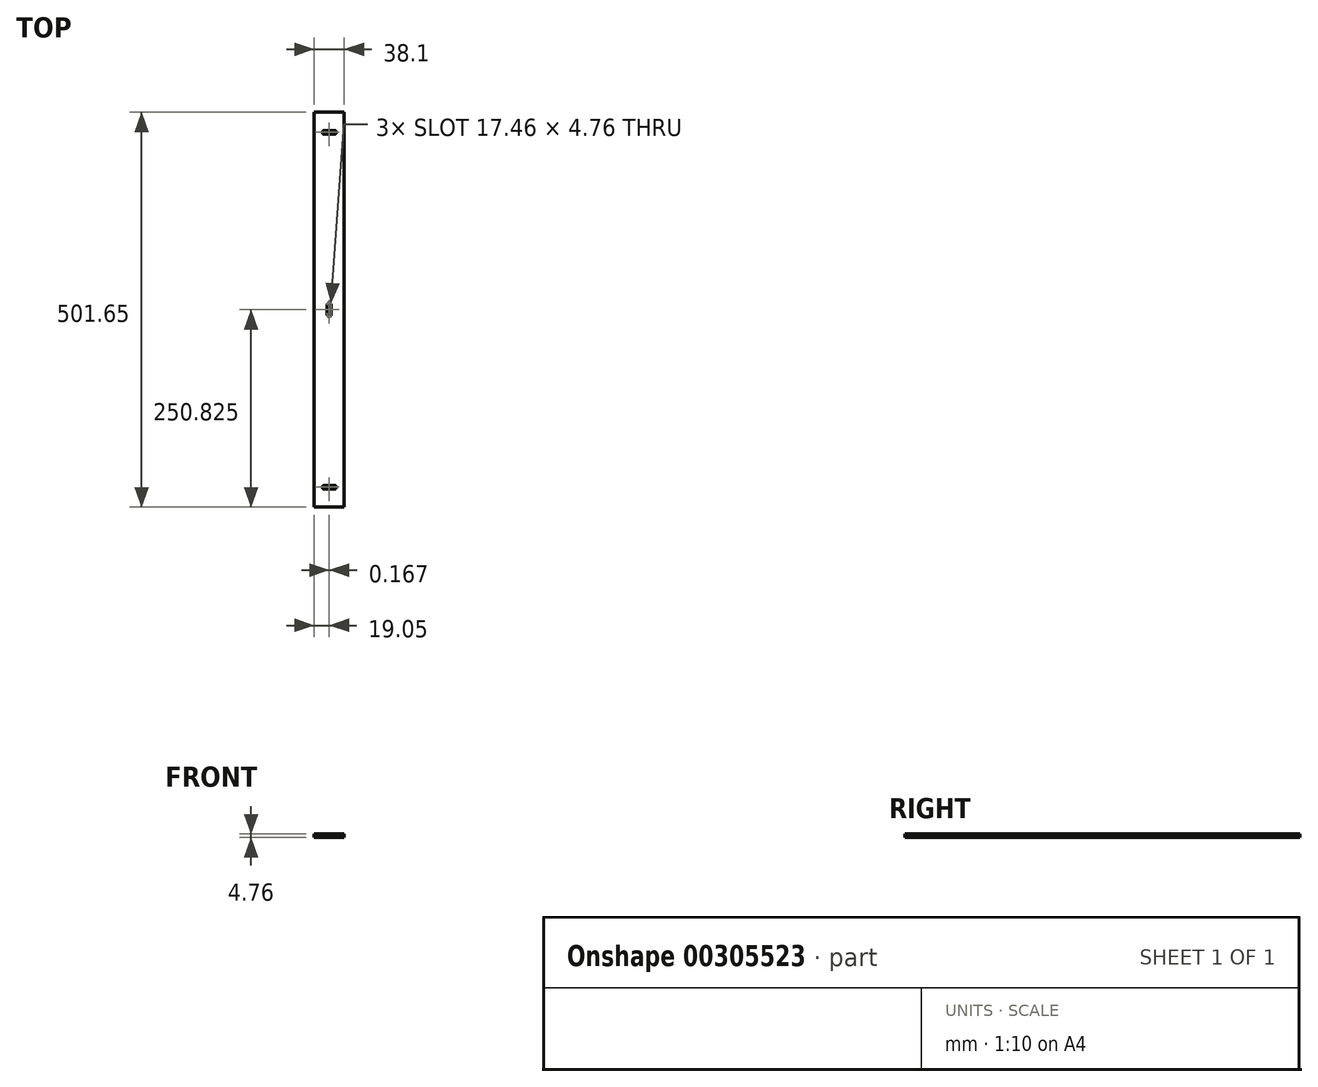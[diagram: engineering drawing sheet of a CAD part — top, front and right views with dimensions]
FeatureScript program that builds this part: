
annotation { "Feature Type Name" : "Feature", "Feature Type Description" : "" }
export const myFeature = defineFeature(function(context is Context, id is Id, definition is map)
    precondition{}
    {
        {
            var Q0;
            Q0=qCreatedBy(makeId("Front.planeOp"),FACE);
            var sketch = newSketch(context, id + "F0", { "sketchPlane" : qUnion([Q0])});
            skLineSegment(sketch, "E0.bottom", {"start": v(0, 0) * mm, "end": v(38.1, 0) * mm});
            skLineSegment(sketch, "E0.top", {"start": v(0, 4.76) * mm, "end": v(38.1, 4.76) * mm});
            skLineSegment(sketch, "E0.left", {"start": v(0, 0) * mm, "end": v(0, 4.76) * mm});
            skLineSegment(sketch, "E0.right", {"start": v(38.1, 0) * mm, "end": v(38.1, 4.76) * mm});
            skSolve(sketch);
        }
        {
            var Q0;
            Q0 = qSketchRegion(id + "F0", true);
            extrude(context, id + "F1", {"entities" : qUnion([Q0]), "depth" : 501.65 * mm});
        }
        {
            var Q0;
            Q0=makeQuery(id+"F1.opExtrude","SWEPT_FACE",FACE,{"disambiguationData":[OSD([sQuery(id+"F0.wireOp",EDGE,"E0.top")])]});
            var sketch = newSketch(context, id + "F2", { "sketchPlane" : qUnion([Q0])});
            skLineSegment(sketch, "E1", {"start": v(0, -250.83) * mm, "end": v(38.1, -250.83) * mm, "construction": true});
            skLineSegment(sketch, "E2", {"start": v(19.05, -250.83) * mm, "end": v(19.05, -257.18) * mm});
            skLineSegment(sketch, "E3", {"start": v(19.22, -476.25) * mm, "end": v(19.22, -476.25) * mm});
            skLineSegment(sketch, "E4.MirrorCS", {"start": v(19.05, -250.83) * mm, "end": v(19.05, -244.47) * mm});
            skLineSegment(sketch, "E5.0.left", {"start": v(16.84, -476.25) * mm, "end": v(16.84, -476.25) * mm});
            skArc(sketch, "E5.2.startCap", {"start": v(21.43, -250.83) * mm, "mid": v(19.05, -253.2) * mm, "end": v(16.67, -250.83) * mm});
            skArc(sketch, "E5.2.endCap", {"start": v(16.67, -244.47) * mm, "mid": v(19.05, -242.1) * mm, "end": v(21.43, -244.47) * mm});
            skLineSegment(sketch, "E5.2.left", {"start": v(16.67, -250.83) * mm, "end": v(16.67, -244.47) * mm});
            skLineSegment(sketch, "E5.2.right", {"start": v(21.43, -250.83) * mm, "end": v(21.43, -244.47) * mm});
            skArc(sketch, "E5.3.startCap", {"start": v(16.67, -250.83) * mm, "mid": v(19.05, -248.44) * mm, "end": v(21.43, -250.83) * mm});
            skArc(sketch, "E5.3.endCap", {"start": v(21.43, -257.18) * mm, "mid": v(19.05, -259.56) * mm, "end": v(16.67, -257.18) * mm});
            skLineSegment(sketch, "E5.3.left", {"start": v(21.43, -250.83) * mm, "end": v(21.43, -257.18) * mm});
            skLineSegment(sketch, "E5.3.right", {"start": v(16.67, -250.83) * mm, "end": v(16.67, -257.18) * mm});
            skPoint(sketch, "E6.startSnap0", {"position": v(16.84, -476.25) * mm});
            skPoint(sketch, "E6.endSnap0", {"position": v(21.6, -476.25) * mm});
            skLineSegment(sketch, "E7", {"start": v(19.22, -476.25) * mm, "end": v(12.87, -476.25) * mm});
            skLineSegment(sketch, "E8.MirrorCS", {"start": v(19.22, -476.25) * mm, "end": v(25.57, -476.25) * mm});
            skLineSegment(sketch, "E9.0.startCap", {"start": v(19.22, -478.63) * mm, "end": v(19.22, -478.63) * mm});
            skArc(sketch, "E9.0.endCap", {"start": v(25.57, -473.87) * mm, "mid": v(27.95, -476.25) * mm, "end": v(25.57, -478.63) * mm});
            skLineSegment(sketch, "E9.0.left", {"start": v(19.22, -473.87) * mm, "end": v(25.57, -473.87) * mm});
            skLineSegment(sketch, "E9.0.right", {"start": v(19.22, -478.63) * mm, "end": v(25.57, -478.63) * mm});
            skLineSegment(sketch, "E9.1.startCap", {"start": v(19.22, -478.63) * mm, "end": v(19.22, -478.63) * mm});
            skArc(sketch, "E9.1.endCap", {"start": v(12.87, -478.63) * mm, "mid": v(10.49, -476.25) * mm, "end": v(12.87, -473.87) * mm});
            skLineSegment(sketch, "E9.1.left", {"start": v(19.22, -478.63) * mm, "end": v(12.87, -478.63) * mm});
            skLineSegment(sketch, "E9.1.right", {"start": v(19.22, -473.87) * mm, "end": v(12.87, -473.87) * mm});
            skArc(sketch, "E10.MirrorCS", {"start": v(12.87, -23.02) * mm, "mid": v(10.49, -25.4) * mm, "end": v(12.87, -27.78) * mm});
            skLineSegment(sketch, "E11.MirrorCS", {"start": v(19.22, -23.02) * mm, "end": v(12.87, -23.02) * mm});
            skLineSegment(sketch, "E12.MirrorCS", {"start": v(19.22, -27.78) * mm, "end": v(12.87, -27.78) * mm});
            skLineSegment(sketch, "E13.MirrorCS", {"start": v(19.22, -27.78) * mm, "end": v(25.57, -27.78) * mm});
            skLineSegment(sketch, "E14.MirrorCS", {"start": v(19.22, -23.02) * mm, "end": v(25.57, -23.02) * mm});
            skArc(sketch, "E15.MirrorCS", {"start": v(25.57, -27.78) * mm, "mid": v(27.95, -25.4) * mm, "end": v(25.57, -23.02) * mm});
            skPoint(sketch, "E5.0.startCap.end.orphan", {"position": v(16.84, -482.6) * mm});
            skPoint(sketch, "E16.orphan", {"position": v(21.6, -482.6) * mm});
            skPoint(sketch, "E5.0.endCap.start.orphan", {"position": v(16.84, -469.9) * mm});
            skPoint(sketch, "E17.orphan", {"position": v(21.6, -469.9) * mm});
            skSolve(sketch);
        }
        {
            var Q0;
            Q0 = qSketchRegion(id + "F2", true);
            extrude(context, id + "F3", {"entities" : qUnion([Q0]), "operationType" : NewBodyOperationType.REMOVE, "oppositeDirection" : true, "depth" : 25.4 * mm});
        }
    });
